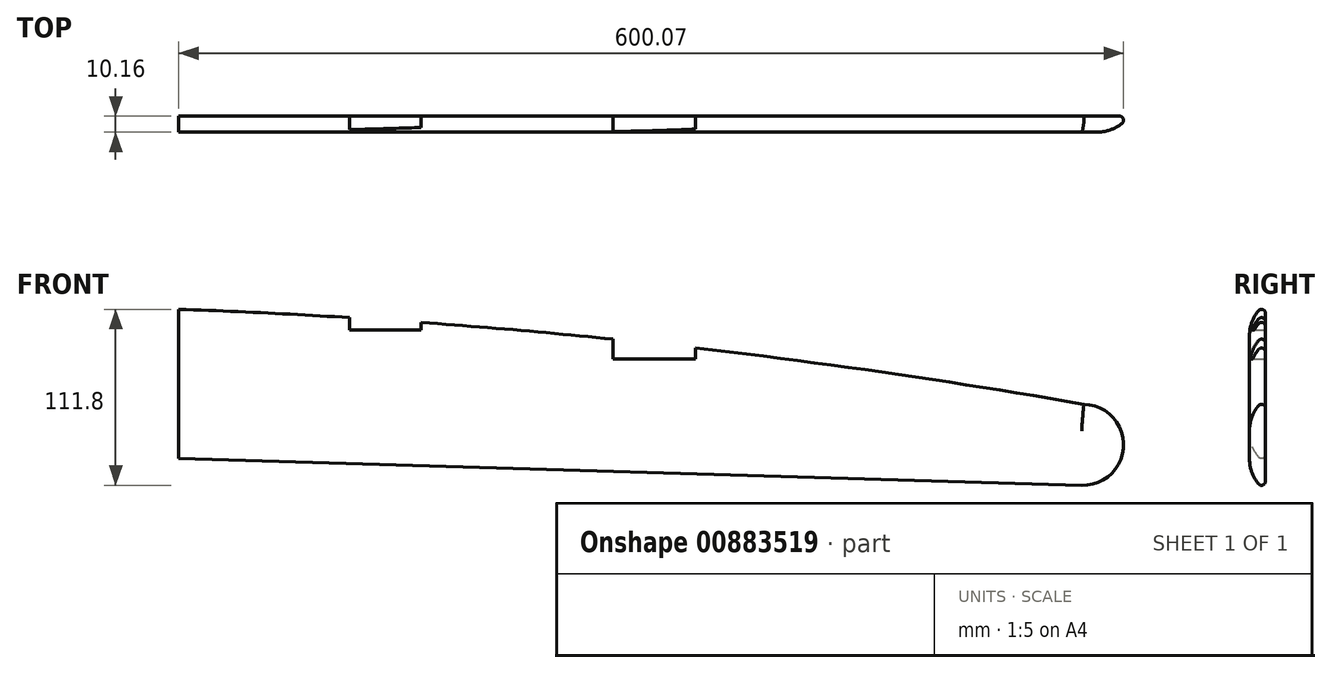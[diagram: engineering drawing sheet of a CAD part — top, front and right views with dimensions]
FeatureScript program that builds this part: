
annotation { "Feature Type Name" : "Feature", "Feature Type Description" : "" }
export const myFeature = defineFeature(function(context is Context, id is Id, definition is map)
    precondition{}
    {
        {
            var Q0;
            Q0=qCreatedBy(makeId("Front.planeOp"),FACE);
            var sketch = newSketch(context, id + "F0", { "sketchPlane" : qUnion([Q0])});
            skPoint(sketch, "E0.start.orphan", {"position": v(0, -101.6) * mm});
            skLineSegment(sketch, "E1", {"start": v(0, -101.6) * mm, "end": v(0, 0) * mm});
            skLineSegment(sketch, "E2", {"start": v(0, -101.6) * mm, "end": v(573.46, -118.61) * mm});
            skArc(sketch, "E3", {"start": v(575.2, -60.32) * mm, "mid": v(288.63, -20.27) * mm, "end": v(0, 0) * mm});
            skArc(sketch, "E4", {"start": v(573.46, -118.61) * mm, "mid": v(603.47, -90.33) * mm, "end": v(575.2, -60.32) * mm});
            skSolve(sketch);
        }
        {
            var Q0;
            Q0 = qSketchRegion(id + "F0", true);
            extrude(context, id + "F1", {"entities" : qUnion([Q0]), "depth" : 10.16 * mm, "offsetDistance" : 25.4 * mm});
        }
        {
            var Q0;
            Q0=makeQuery(id+"F1.opExtrude","CAP_EDGE",EDGE,{"disambiguationData":[OSD([sQuery(id+"F0.wireOp",EDGE,"E3")])],"isStart":false});
            var Q1;
            Q1=makeQuery(id+"F1.opExtrude","CAP_EDGE",EDGE,{"disambiguationData":[OSD([sQuery(id+"F0.wireOp",EDGE,"E4")])],"isStart":false});
            var Q2;
            Q2=makeQuery(id+"F1.opExtrude","CAP_EDGE",EDGE,{"disambiguationData":[OSD([sQuery(id+"F0.wireOp",EDGE,"E2")])],"isStart":false});
            fillet(context, id + "F2", {"entities" : qUnion([Q0, Q1, Q2]), "radius" : 25.4 * mm, "tangentPropagation" : true, "allowEdgeOverflow" : false});
        }
        {
            var Q0;
            {var subQ0=sQuery(id+"F0.wireOp",EDGE,"E2");Q0=makeQuery(id+"F2.opFillet","BLEND_EDGE",EDGE,{"blendedFrom":[makeQuery(id+"F1.opExtrude","CAP_EDGE",EDGE,{"disambiguationData":[OSD([subQ0])],"isStart":false}),makeQuery(id+"F1.opExtrude","CAP_FACE",FACE,{"disambiguationData":[OSD([sQuery(id+"F0.wireOp",EDGE,"E1"),subQ0,sQuery(id+"F0.wireOp",EDGE,"E3"),sQuery(id+"F0.wireOp",EDGE,"E4")])],"isStart":true})],"blendedInto":[makeQuery(id+"F1.opExtrude","CAP_FACE",FACE,{"disambiguationData":[OSD([sQuery(id+"F0.wireOp",EDGE,"E1"),subQ0,sQuery(id+"F0.wireOp",EDGE,"E3"),sQuery(id+"F0.wireOp",EDGE,"E4")])],"isStart":true})]});}
            var Q1;
            {var subQ0=sQuery(id+"F0.wireOp",EDGE,"E4");Q1=makeQuery(id+"F2.opFillet","BLEND_EDGE",EDGE,{"blendedFrom":[makeQuery(id+"F1.opExtrude","CAP_EDGE",EDGE,{"disambiguationData":[OSD([subQ0])],"isStart":false}),makeQuery(id+"F1.opExtrude","CAP_FACE",FACE,{"disambiguationData":[OSD([sQuery(id+"F0.wireOp",EDGE,"E1"),sQuery(id+"F0.wireOp",EDGE,"E2"),sQuery(id+"F0.wireOp",EDGE,"E3"),subQ0])],"isStart":true})],"blendedInto":[makeQuery(id+"F1.opExtrude","CAP_FACE",FACE,{"disambiguationData":[OSD([sQuery(id+"F0.wireOp",EDGE,"E1"),sQuery(id+"F0.wireOp",EDGE,"E2"),sQuery(id+"F0.wireOp",EDGE,"E3"),subQ0])],"isStart":true})]});}
            var Q2;
            {var subQ0=sQuery(id+"F0.wireOp",EDGE,"E3");Q2=makeQuery(id+"F2.opFillet","BLEND_EDGE",EDGE,{"blendedFrom":[makeQuery(id+"F1.opExtrude","CAP_EDGE",EDGE,{"disambiguationData":[OSD([subQ0])],"isStart":false}),makeQuery(id+"F1.opExtrude","CAP_FACE",FACE,{"disambiguationData":[OSD([sQuery(id+"F0.wireOp",EDGE,"E1"),sQuery(id+"F0.wireOp",EDGE,"E2"),subQ0,sQuery(id+"F0.wireOp",EDGE,"E4")])],"isStart":true})],"blendedInto":[makeQuery(id+"F1.opExtrude","CAP_FACE",FACE,{"disambiguationData":[OSD([sQuery(id+"F0.wireOp",EDGE,"E1"),sQuery(id+"F0.wireOp",EDGE,"E2"),subQ0,sQuery(id+"F0.wireOp",EDGE,"E4")])],"isStart":true})]});}
            fillet(context, id + "F3", {"entities" : qUnion([Q0, Q1, Q2]), "radius" : 2.54 * mm, "tangentPropagation" : true, "allowEdgeOverflow" : false});
        }
        {
            var Q0;
            Q0=qCreatedBy(makeId("Front.planeOp"),FACE);
            var sketch = newSketch(context, id + "F4", { "sketchPlane" : qUnion([Q0])});
            skLineSegment(sketch, "E5.bottom", {"start": v(108.5, 0) * mm, "end": v(153.84, 0) * mm});
            skLineSegment(sketch, "E5.top", {"start": v(108.5, -16.7) * mm, "end": v(153.84, -16.7) * mm});
            skLineSegment(sketch, "E5.left", {"start": v(108.5, 0) * mm, "end": v(108.5, -16.7) * mm});
            skLineSegment(sketch, "E5.right", {"start": v(153.84, 0) * mm, "end": v(153.84, -16.7) * mm});
            skLineSegment(sketch, "E6.bottom", {"start": v(275.73, -18.84) * mm, "end": v(328.34, -18.84) * mm});
            skLineSegment(sketch, "E6.top", {"start": v(275.73, -35.1) * mm, "end": v(328.34, -35.1) * mm});
            skLineSegment(sketch, "E6.left", {"start": v(275.73, -18.84) * mm, "end": v(275.73, -35.1) * mm});
            skLineSegment(sketch, "E6.right", {"start": v(328.34, -18.84) * mm, "end": v(328.34, -35.1) * mm});
            skSolve(sketch);
        }
        {
            var Q0;
            Q0 = qSketchRegion(id + "F4", true);
            extrude(context, id + "F5", {"entities" : qUnion([Q0]), "operationType" : NewBodyOperationType.REMOVE, "depth" : 25.4 * mm, "offsetDistance" : 25.4 * mm});
        }
    });
